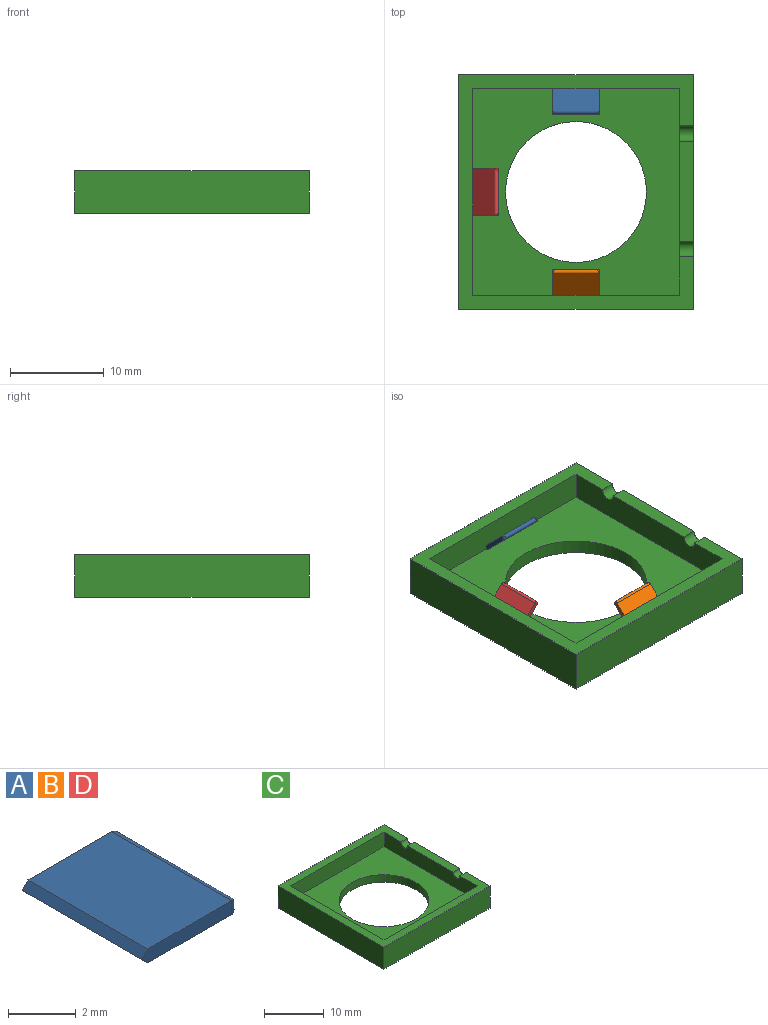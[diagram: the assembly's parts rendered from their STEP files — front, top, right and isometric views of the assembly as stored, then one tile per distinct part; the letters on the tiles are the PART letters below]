
ASSEMBLY  parts=4 mates=3
PART A: 9 faces, bbox 4x5x0.5 mm
  f0: plane 3.75x0.5mm, normal (0,-1,0), area 1.8mm2, adj f1,f3,f6,f7,f8
  f1: plane 5x3.5mm, normal (0,0,-1), area 17.5mm2, adj f0,f2,f5,f8
  f2: plane 3.75x0.5mm, normal (0,1,0), area 1.8mm2, adj f1,f3,f4,f7,f8
  f3: plane 5x3.5mm, normal (0,0,1), area 17.5mm2, adj f0,f2,f5,f7
  f4: cylinder r=0.25mm len=0.5mm, axis (0,0,1), area 0.1mm2, adj f2,f5
  f5: cylinder r=0.25mm len=5mm, axis (0,-1,0), area 3.7mm2, adj f1,f3,f4,f6
  f6: cylinder r=0.25mm len=0.5mm, axis (0,0,-1), area 0.1mm2, adj f0,f5
  f7: plane 5x0.25mm, normal (-0.71,0,0.71), area 1.8mm2, adj f0,f2,f3,f8
  f8: plane 5x0.25mm, normal (-0.71,0,-0.71), area 1.8mm2, adj f0,f1,f2,f7
PART B: same geometry as A
PART C: 15 faces, bbox 25x25x4.5 mm
  f0: plane 25x25mm, normal (0,0,1), area 120.1mm2, adj f1,f4,f5,f6,f8,f9,f10,f11
  f1: plane 25x4.5mm, normal (1,0,0), area 110.4mm2, adj f0,f2,f4,f5,f7,f13,f14
  f2: plane 10.66x1.5mm, normal (0,0,1), area 16mm2, adj f1,f9,f13,f14
  f3: cylinder r=7.5mm len=15mm, axis (0,0,1), area 70.7mm2, adj f7,f12
  f4: plane 25x4.5mm, normal (0,-1,0), area 112.5mm2, adj f0,f1,f6,f7
  f5: plane 25x4.5mm, normal (0,1,0), area 112.5mm2, adj f0,f1,f6,f7
  f6: plane 25x4.5mm, normal (-1,0,0), area 112.5mm2, adj f0,f4,f5,f7
  f7: plane 25x25mm, normal (0,0,-1), area 448.3mm2, adj f1,f3,f4,f5,f6
  f8: plane 22x3mm, normal (0,1,0), area 66mm2, adj f0,f9,f11,f12
  f9: plane 22x3mm, normal (-1,0,0), area 63.9mm2, adj f0,f2,f8,f10,f12,f13,f14
  f10: plane 22x3mm, normal (0,-1,0), area 66mm2, adj f0,f9,f11,f12
  f11: plane 22x3mm, normal (1,0,0), area 66mm2, adj f0,f8,f10,f12
  f12: plane 22x22mm, normal (0,0,1), area 307.3mm2, adj f3,f8,f9,f10,f11
  f13: cylinder r=0.81mm len=1.63mm, axis (1,0,0), area 3.8mm2, adj f0,f1,f2,f9
  f14: cylinder r=0.81mm len=1.63mm, axis (1,0,0), area 3.8mm2, adj f0,f1,f2,f9
PART D: same geometry as A
PLACE A rot(axis=(-0.36,-0.36,-0.86),98.4deg) t=(-5.58,9.22,3.59)mm
PLACE B rot(axis=(0.36,-0.36,0.86),98.4deg) t=(-5.58,-10.66,3.59)mm
PLACE C t=(-5.58,-0.72,0.5)mm
PLACE D rot(axis=(0,-1,0),45deg) t=(-15.52,-0.72,3.59)mm
MATE fastened D.f8 <-> C.f12  axis (0,0,-1) through (-16.58,-0.72,2)mm
MATE fastened B.f8 <-> C.f12  axis (0,0,-1) through (-5.58,-11.72,2)mm
MATE fastened A.f8 <-> C.f12  axis (0,0,-1) through (-5.58,10.28,2)mm
